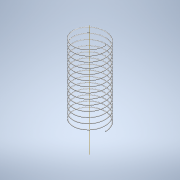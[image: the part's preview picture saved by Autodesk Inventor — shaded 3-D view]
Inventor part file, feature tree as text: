
AUTODESK INVENTOR PART (.ipt)
format: ipt  version: 2020 (Build 240168000, 168)  size: 336,384 bytes
history: native  units: mm
features: helix x1, other x1, sketch x1
ambient origin geometry x8: Origin, YZ Plane, XZ Plane, XY Plane, X Axis, Y Axis, Z Axis, Center Point
bodies: Solid1 (feature_tree)
feature tree (3):
  helix  "Coil1"  [1 undecoded]
  other  "Work Axis1"
  sketch  "Sketch1"  dims[d1=0.3mm d2=10.0mm d3=32.697mm d4=140.0mm d5=0.0mm d6=90.0deg d7=90.0deg d8=0.0mm d9=0.0mm]
note: 1 required parameter value undecoded (feature->parameter linkage not recoverable at this tier; creation-order binding heuristic only, values carry confidence <= 0.55)
